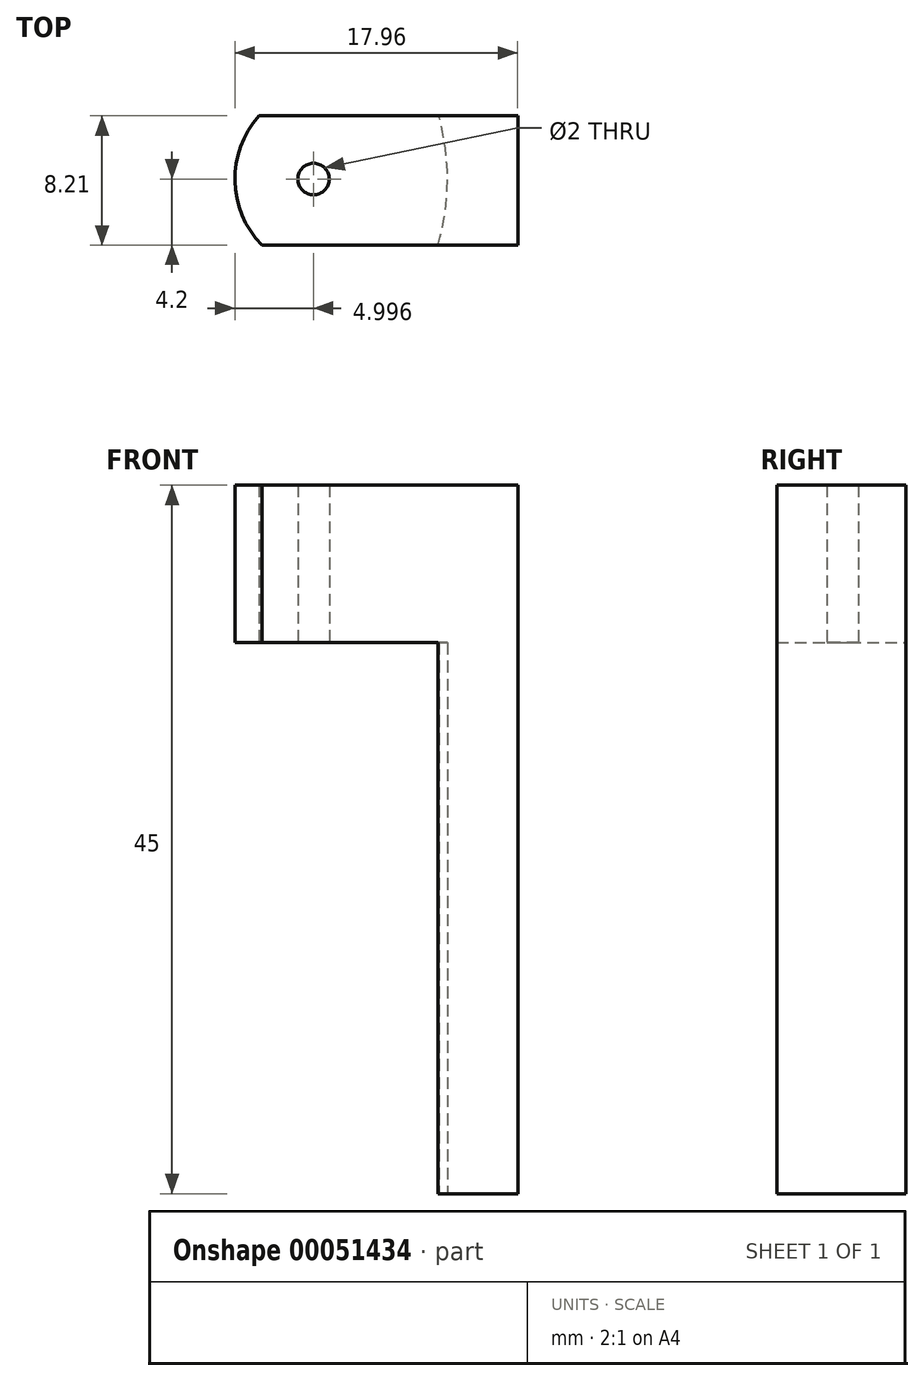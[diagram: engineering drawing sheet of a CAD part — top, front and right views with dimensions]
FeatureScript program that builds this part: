
annotation { "Feature Type Name" : "Feature", "Feature Type Description" : "" }
export const myFeature = defineFeature(function(context is Context, id is Id, definition is map)
    precondition{}
    {
        {
            var Q0;
            Q0=qCreatedBy(makeId("Top.planeOp"),FACE);
            var sketch = newSketch(context, id + "F0", { "sketchPlane" : qUnion([Q0])});
            skCircle(sketch, "E0", {"center": v(-35.82, 0) * mm, "radius": 15 * mm});
            skLineSegment(sketch, "E1", {"start": v(-21.37, 4) * mm, "end": v(-16.36, 4) * mm});
            skLineSegment(sketch, "E2", {"start": v(-16.36, 4) * mm, "end": v(-16.36, -4.2) * mm});
            skLineSegment(sketch, "E3", {"start": v(-16.36, -4.2) * mm, "end": v(-21.42, -4.2) * mm});
            skSolve(sketch);
        }
        {
            var Q0;
            {var subQ1=sQuery(id+"F0.wireOp",EDGE,"E1");Q0=makeQuery(id+"F0.imprint","IMPRINT",FACE,{"disambiguationData":[TD([[makeQuery(id+"F0.imprint","IMPRINT",EDGE,{"derivedFrom":subQ1}),-1.0]])]});}
            extrude(context, id + "F1", {"entities" : qUnion([Q0]), "depth" : 35 * mm});
        }
        {
            var Q0;
            Q0=makeQuery(id+"F1.opExtrude","CAP_FACE",FACE,{"disambiguationData":[OSD([sQuery(id+"F0.wireOp",EDGE,"E0"),sQuery(id+"F0.wireOp",EDGE,"E1"),sQuery(id+"F0.wireOp",EDGE,"E2"),sQuery(id+"F0.wireOp",EDGE,"E3")])],"isStart":false});
            var sketch = newSketch(context, id + "F2", { "sketchPlane" : qUnion([Q0])});
            skLineSegment(sketch, "E4.bottom", {"start": v(-16.36, 4) * mm, "end": v(-49.22, 4) * mm});
            skLineSegment(sketch, "E4.top", {"start": v(-16, -4.2) * mm, "end": v(-49.22, -4.2) * mm});
            skLineSegment(sketch, "E4.right", {"start": v(-49.22, 4) * mm, "end": v(-49.22, -4.2) * mm});
            skCircle(sketch, "E5", {"center": v(-29.32, 0) * mm, "radius": 1 * mm});
            skArc(sketch, "E6", {"start": v(-32.8, 4) * mm, "mid": v(-34.32, -0.13) * mm, "end": v(-32.6, -4.2) * mm});
            skSolve(sketch);
        }
        {
            var Q0;
            {var subQ8=sQuery(id+"F2.wireOp",EDGE,"E4.left");Q0=makeQuery(id+"F2.imprint","IMPRINT",FACE,{"disambiguationData":[TD([[makeQuery(id+"F2.imprint","IMPRINT",EDGE,{"derivedFrom":subQ8}),-1.0]])]});}
            var Q1;
            Q1=makeQuery(id+"F2.imprint","IMPRINT",FACE,{"disambiguationData":[TD([[makeQuery(id+"F2.imprint","IMPRINT",EDGE,{"derivedFrom":sQuery(id+"F2.wireOp",EDGE,"E5")}),-1.0]])]});
            var Q2;
            {var subQ1=makeQuery(id+"F1.opExtrude","CAP_EDGE",EDGE,{"disambiguationData":[OSD([sQuery(id+"F0.wireOp",EDGE,"E0")])],"isStart":false});Q2=makeQuery(id+"F2.imprint","IMPRINT",FACE,{"disambiguationData":[TD([[makeQuery(id+"F2.imprint","IMPRINT",EDGE,{"derivedFrom":subQ1}),-1.0]])]});}
            extrude(context, id + "F3", {"entities" : qUnion([Q0, Q1, Q2]), "operationType" : NewBodyOperationType.ADD, "depth" : 10 * mm});
        }
    });
